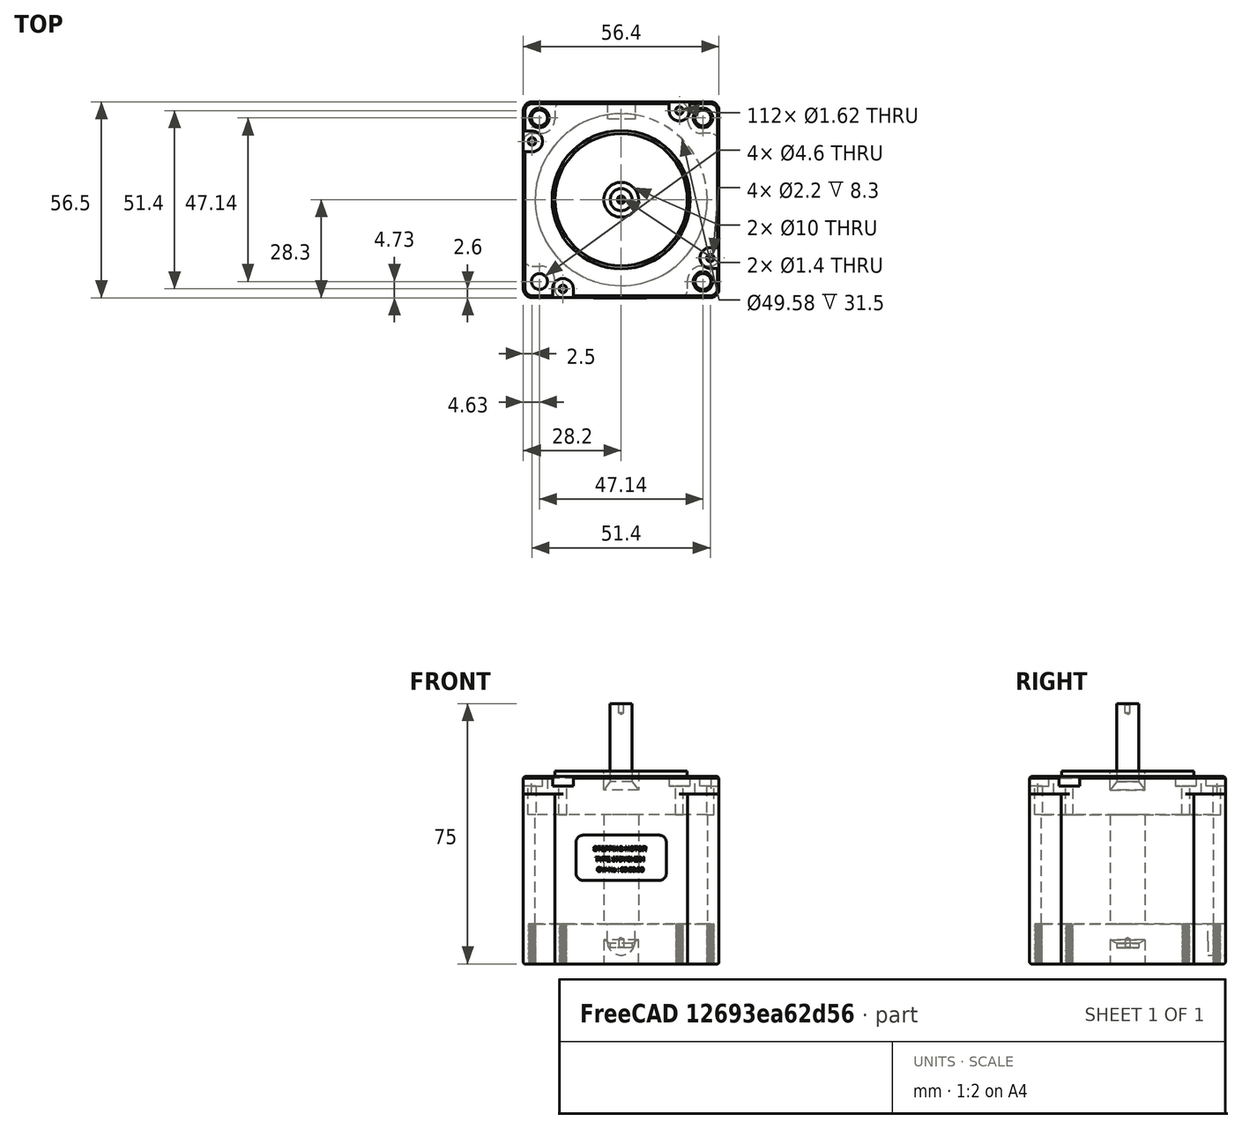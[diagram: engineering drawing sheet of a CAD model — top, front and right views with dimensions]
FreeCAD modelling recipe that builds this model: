
FCSTD DOCUMENT  (FreeCAD 1.0R38641 +468 (Git))
Label: nema23
License: All rights reserved
LicenseURL: https://en.wikipedia.org/wiki/All_rights_reserved
objects: Part::Feature×5, Part::MultiFuse×2, App::Part×1
note: 7 computed .brp shape members not serialized (recipe doc carries the construction recipe); baked Part::Feature solids carry a one-line shape summary decoded from their .brp

FEATURE [Part::Feature] Part__Feature  label="Up"
  shape: bbox 56.4 x 56.4 x 12.6 mm, 78 faces (baked)
FEATURE [Part::Feature] Part__Feature001  label="Axe"
  shape: bbox 10 x 10 x 70.4 mm, 13 faces (baked)
FEATURE [Part::Feature] Part__Feature002  label="Bottom"
  shape: bbox 56.81 x 56.81 x 11.93 mm, 535 faces (baked)
FEATURE [Part::Feature] Part__Feature003  label="Middle"
  shape: bbox 56.4 x 56.4 x 31.5 mm, 27 faces (baked)
FEATURE [Part::Feature] Part__Feature008  label="Sticker"
  Placement = pos=(0,-28.2,-24.4) rot=(1,0,0;1.5708rad)
  shape: bbox 26 x 0.1 x 13 mm, 831 faces (baked)
FEATURE [Part::MultiFuse] Fusion
  Shapes = -> [Part__Feature008,Part__Feature003]
FEATURE [Part::MultiFuse] Fusion001
  Shapes = -> [Part__Feature008,Part__Feature003,Part__Feature,Part__Feature001,Part__Feature002,Fusion]
FEATURE [App::Part] nema23_57byg201
  Group = -> [Fusion,Part__Feature,Part__Feature003,Part__Feature001,Part__Feature002,Part__Feature008,Fusion001]
  Origin = -> Origin
